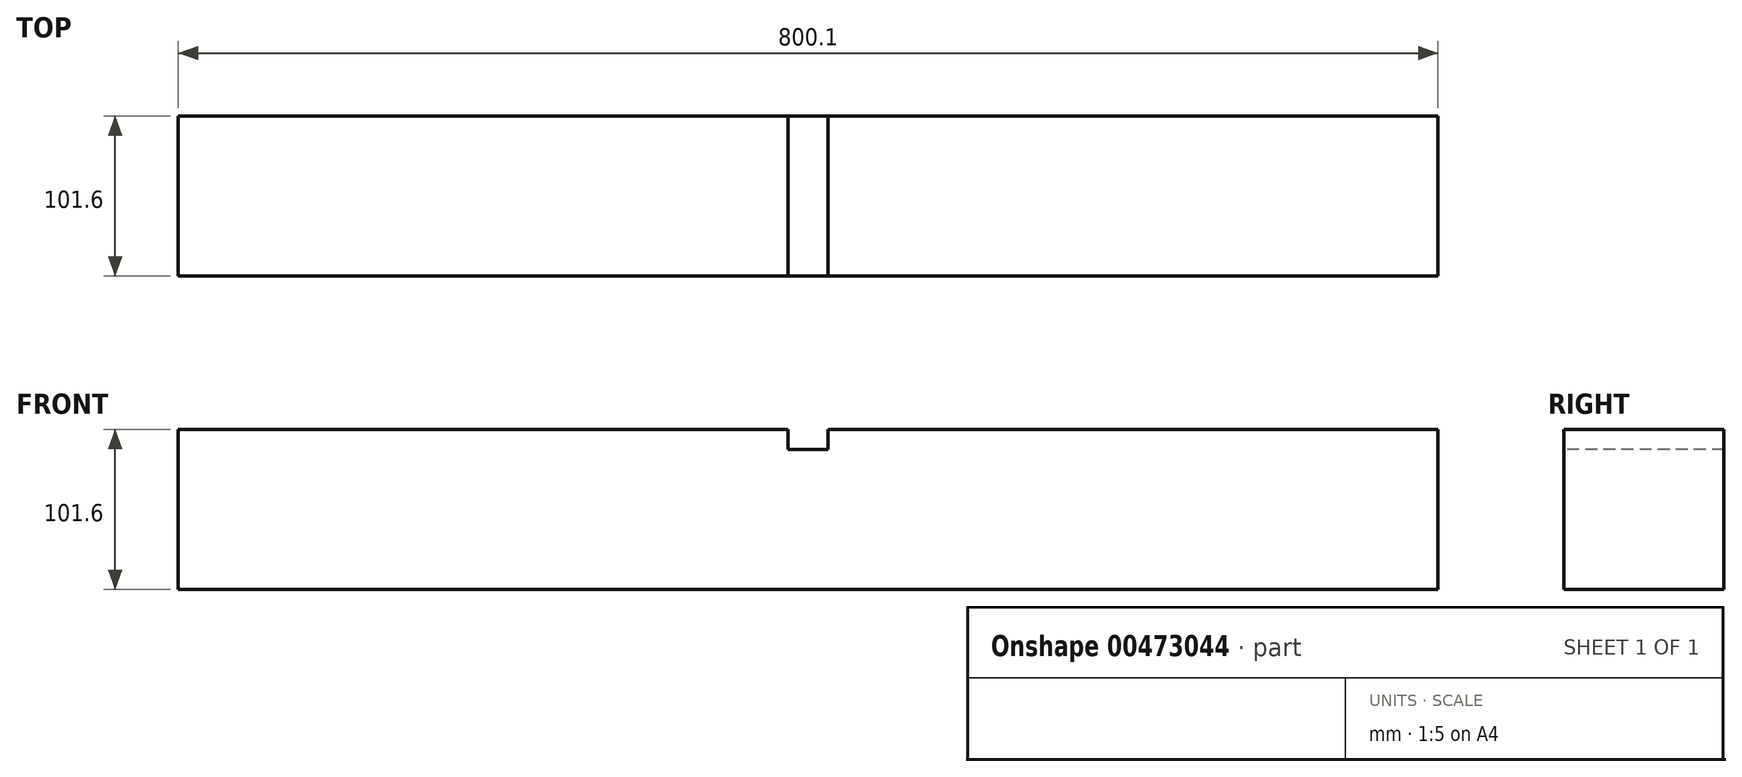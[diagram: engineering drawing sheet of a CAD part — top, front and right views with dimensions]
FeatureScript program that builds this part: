
annotation { "Feature Type Name" : "Feature", "Feature Type Description" : "" }
export const myFeature = defineFeature(function(context is Context, id is Id, definition is map)
    precondition{}
    {
        {
            var Q0;
            Q0=qCreatedBy(makeId("Front.planeOp"),FACE);
            var sketch = newSketch(context, id + "F0", { "sketchPlane" : qUnion([Q0])});
            skLineSegment(sketch, "E0.bottom", {"start": v(400.05, 50.8) * mm, "end": v(-400.05, 50.8) * mm});
            skLineSegment(sketch, "E0.top", {"start": v(400.05, -50.8) * mm, "end": v(-400.05, -50.8) * mm});
            skLineSegment(sketch, "E0.left", {"start": v(400.05, 50.8) * mm, "end": v(400.05, -50.8) * mm});
            skLineSegment(sketch, "E0.right", {"start": v(-400.05, 50.8) * mm, "end": v(-400.05, -50.8) * mm});
            skPoint(sketch, "E0.middle", {"position": v(0, 0) * mm});
            skSolve(sketch);
        }
        {
            var Q0;
            Q0=makeQuery(id+"F0.imprint","IMPRINT",FACE,{"disambiguationData":[TD([[makeQuery(id+"F0.imprint","IMPRINT",EDGE,{"derivedFrom":sQuery(id+"F0.wireOp",EDGE,"E0.bottom")}),1.0]])]});
            extrude(context, id + "F1", {"entities" : qUnion([Q0]), "depth" : 101.6 * mm});
        }
        {
            var Q0;
            Q0=makeQuery(id+"F1.opExtrude","CAP_FACE",FACE,{"disambiguationData":[OSD([sQuery(id+"F0.wireOp",EDGE,"E0.bottom"),sQuery(id+"F0.wireOp",EDGE,"E0.top"),sQuery(id+"F0.wireOp",EDGE,"E0.left"),sQuery(id+"F0.wireOp",EDGE,"E0.right")])],"isStart":false});
            var sketch = newSketch(context, id + "F2", { "sketchPlane" : qUnion([Q0])});
            skLineSegment(sketch, "E1", {"start": v(0, 0) * mm, "end": v(0, 50.8) * mm});
            skLineSegment(sketch, "E2.bottom", {"start": v(12.7, 63.5) * mm, "end": v(-12.7, 63.5) * mm});
            skLineSegment(sketch, "E2.top", {"start": v(12.7, 38.1) * mm, "end": v(-12.7, 38.1) * mm});
            skLineSegment(sketch, "E2.left", {"start": v(12.7, 63.5) * mm, "end": v(12.7, 38.1) * mm});
            skLineSegment(sketch, "E2.right", {"start": v(-12.7, 63.5) * mm, "end": v(-12.7, 38.1) * mm});
            skPoint(sketch, "E2.middle", {"position": v(0, 50.8) * mm});
            skSolve(sketch);
        }
        {
            var Q0;
            Q0 = qSketchRegion(id + "F2", true);
            extrude(context, id + "F3", {"entities" : qUnion([Q0]), "operationType" : NewBodyOperationType.REMOVE, "endBound" : BoundingType.THROUGH_ALL, "oppositeDirection" : true, "depth" : 25.4 * mm});
        }
    });
